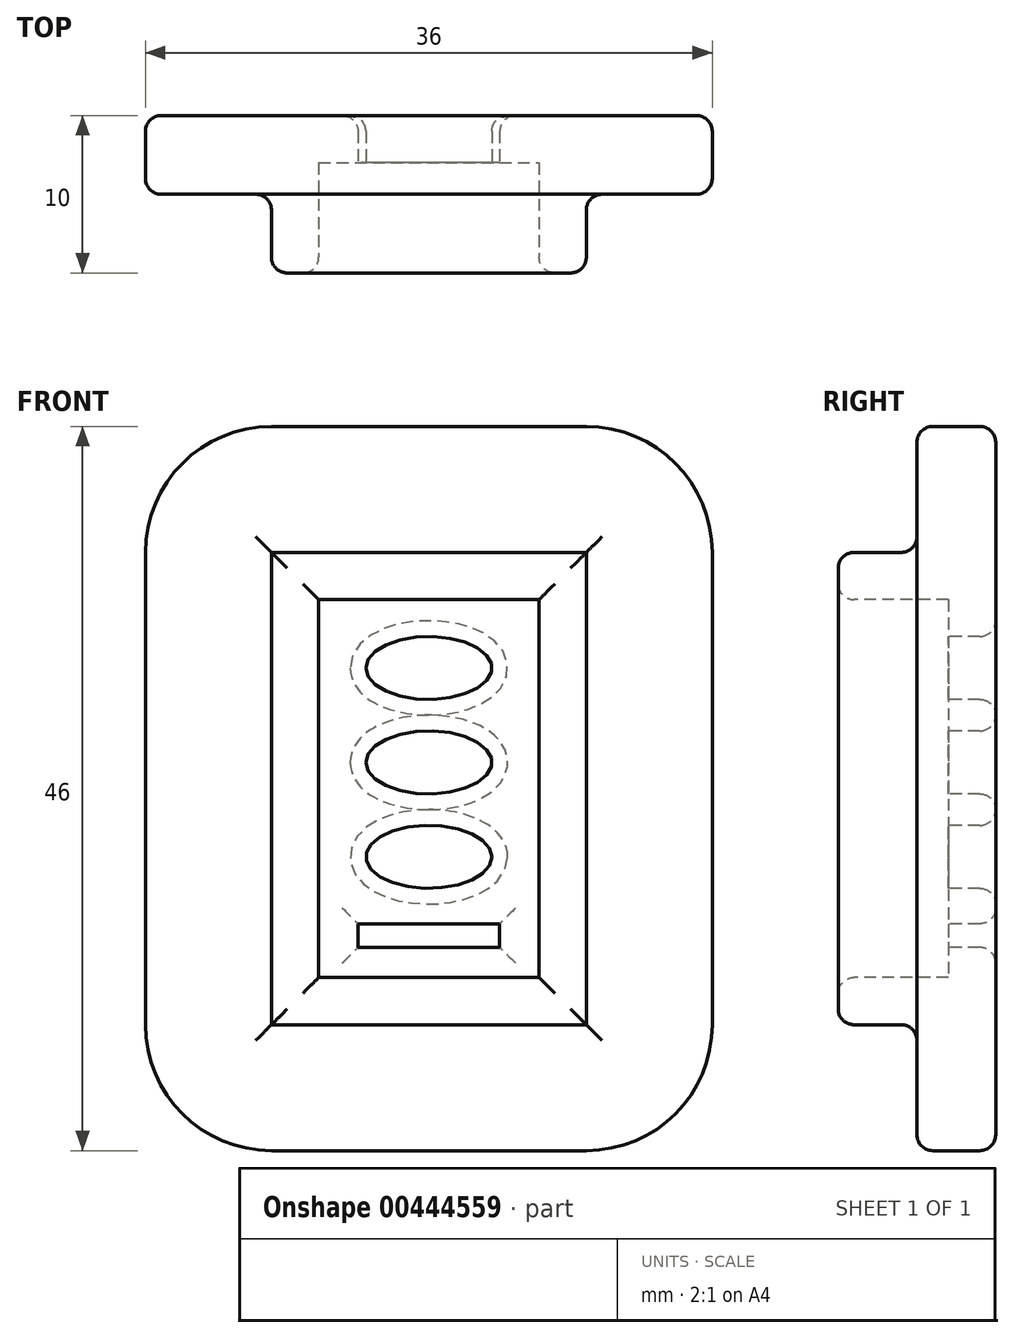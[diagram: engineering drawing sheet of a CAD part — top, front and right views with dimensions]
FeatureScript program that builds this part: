
annotation { "Feature Type Name" : "Feature", "Feature Type Description" : "" }
export const myFeature = defineFeature(function(context is Context, id is Id, definition is map)
    precondition{}
    {
        {
            var Q0;
            Q0=qCreatedBy(makeId("Front.planeOp"),FACE);
            var sketch = newSketch(context, id + "F0", { "sketchPlane" : qUnion([Q0])});
            skLineSegment(sketch, "E0.bottom", {"start": v(-10, -23) * mm, "end": v(10, -23) * mm});
            skLineSegment(sketch, "E0.top", {"start": v(-10, 23) * mm, "end": v(10, 23) * mm});
            skLineSegment(sketch, "E0.left", {"start": v(-18, -15) * mm, "end": v(-18, 15) * mm});
            skLineSegment(sketch, "E0.right", {"start": v(18, -15) * mm, "end": v(18, 15) * mm});
            skPoint(sketch, "E0.middle", {"position": v(0, 0) * mm});
            skPoint(sketch, "E1.visualSharp", {"position": v(-18, 23) * mm});
            skArc(sketch, "E1.filletArc", {"start": v(-10, 23) * mm, "mid": v(-15.66, 20.66) * mm, "end": v(-18, 15) * mm});
            skPoint(sketch, "E2.visualSharp", {"position": v(18, 23) * mm});
            skArc(sketch, "E2.filletArc", {"start": v(18, 15) * mm, "mid": v(15.66, 20.66) * mm, "end": v(10, 23) * mm});
            skPoint(sketch, "E3.visualSharp", {"position": v(18, -23) * mm});
            skArc(sketch, "E3.filletArc", {"start": v(10, -23) * mm, "mid": v(15.66, -20.66) * mm, "end": v(18, -15) * mm});
            skPoint(sketch, "E4.visualSharp", {"position": v(-18, -23) * mm});
            skArc(sketch, "E4.filletArc", {"start": v(-18, -15) * mm, "mid": v(-15.66, -20.66) * mm, "end": v(-10, -23) * mm});
            skSolve(sketch);
        }
        {
            var Q0;
            Q0=makeQuery(id+"F0.imprint","IMPRINT",FACE,{"disambiguationData":[TD([[makeQuery(id+"F0.imprint","IMPRINT",EDGE,{"derivedFrom":sQuery(id+"F0.wireOp",EDGE,"E0.bottom")}),1.0]])]});
            cPlane(context, id + "F1", {"entities" : qUnion([Q0]), "cplaneType" : CPlaneType.OFFSET, "offset" : 5 * mm, "width" : 150 * mm, "height" : 150 * mm});
        }
        {
            var Q0;
            Q0=qCreatedBy(id+"F1.planeOp",FACE);
            var sketch = newSketch(context, id + "F2", { "sketchPlane" : qUnion([Q0])});
            skLineSegment(sketch, "E5.bottom", {"start": v(-10, 15) * mm, "end": v(10, 15) * mm});
            skLineSegment(sketch, "E5.top", {"start": v(-10, -15) * mm, "end": v(10, -15) * mm});
            skLineSegment(sketch, "E5.left", {"start": v(-10, 15) * mm, "end": v(-10, -15) * mm});
            skLineSegment(sketch, "E5.right", {"start": v(10, 15) * mm, "end": v(10, -15) * mm});
            skPoint(sketch, "E5.middle", {"position": v(0, 0) * mm});
            skSolve(sketch);
        }
        {
            var Q0;
            Q0 = qSketchRegion(id + "F2", true);
            extrude(context, id + "F3", {"entities" : qUnion([Q0]), "oppositeDirection" : true, "depth" : 5 * mm});
        }
        {
            var Q0;
            Q0=makeQuery(id+"F3.opExtrude","CAP_FACE",FACE,{"disambiguationData":[OSD([sQuery(id+"F2.wireOp",EDGE,"E5.bottom"),sQuery(id+"F2.wireOp",EDGE,"E5.top"),sQuery(id+"F2.wireOp",EDGE,"E5.left"),sQuery(id+"F2.wireOp",EDGE,"E5.right")])],"isStart":true});
            var Q1;
            Q1=makeQuery(id+"F0.imprint","IMPRINT",FACE,{"disambiguationData":[TD([[makeQuery(id+"F0.imprint","IMPRINT",EDGE,{"derivedFrom":sQuery(id+"F0.wireOp",EDGE,"E0.bottom")}),1.0]])]});
            extrude(context, id + "F4", {"entities" : qUnion([Q0, Q1]), "operationType" : NewBodyOperationType.ADD, "oppositeDirection" : true, "depth" : 5 * mm});
        }
        {
            var Q0;
            Q0=makeQuery(id+"F3.opExtrude","CAP_FACE",FACE,{"disambiguationData":[OSD([sQuery(id+"F2.wireOp",EDGE,"E5.bottom"),sQuery(id+"F2.wireOp",EDGE,"E5.top"),sQuery(id+"F2.wireOp",EDGE,"E5.left"),sQuery(id+"F2.wireOp",EDGE,"E5.right")])],"isStart":true});
            shell(context, id + "F5", {"entities" : qUnion([Q0]), "thickness" : 3 * mm});
        }
        {
            var Q0;
            Q0=makeQuery(id+"F5.opShell","OFFSET_FACE",FACE,{"disambiguationData":[OSD([sQuery(id+"F0.wireOp",EDGE,"E0.bottom"),sQuery(id+"F0.wireOp",EDGE,"E0.top"),sQuery(id+"F0.wireOp",EDGE,"E0.left"),sQuery(id+"F0.wireOp",EDGE,"E0.right"),sQuery(id+"F0.wireOp",EDGE,"E1.filletArc"),sQuery(id+"F0.wireOp",EDGE,"E2.filletArc"),sQuery(id+"F0.wireOp",EDGE,"E3.filletArc"),sQuery(id+"F0.wireOp",EDGE,"E4.filletArc")])]});
            var sketch = newSketch(context, id + "F6", { "sketchPlane" : qUnion([Q0])});
            skLineSegment(sketch, "E6.bottom", {"start": v(4.5, -8.59) * mm, "end": v(-4.5, -8.59) * mm});
            skLineSegment(sketch, "E6.top", {"start": v(4.5, -10.09) * mm, "end": v(-4.5, -10.09) * mm});
            skLineSegment(sketch, "E6.left", {"start": v(4.5, -8.59) * mm, "end": v(4.5, -10.09) * mm});
            skLineSegment(sketch, "E6.right", {"start": v(-4.5, -8.59) * mm, "end": v(-4.5, -10.09) * mm});
            skPoint(sketch, "E6.middle", {"position": v(0, -9.34) * mm});
            skEllipse(sketch, "E7", {"center": v(0, -4.34) * mm, "majorRadius": 4 * mm, "minorRadius": 2 * mm, "majorAxis": v(1, 0)});
            skEllipse(sketch, "E8", {"center": v(0, 1.66) * mm, "majorRadius": 4 * mm, "minorRadius": 2 * mm, "majorAxis": v(-1, 0)});
            skEllipse(sketch, "E9", {"center": v(0, 7.66) * mm, "majorRadius": 4 * mm, "minorRadius": 2 * mm, "majorAxis": v(-1, 0)});
            skSolve(sketch);
        }
        {
            var Q0;
            Q0=makeQuery(id+"F6.imprint","IMPRINT",FACE,{"disambiguationData":[TD([[makeQuery(id+"F6.imprint","IMPRINT",EDGE,{"derivedFrom":sQuery(id+"F6.wireOp",EDGE,"E6.bottom")}),1.0]])]});
            var Q1;
            Q1=makeQuery(id+"F6.imprint","IMPRINT",FACE,{"disambiguationData":[TD([[makeQuery(id+"F6.imprint","IMPRINT",EDGE,{"derivedFrom":sQuery(id+"F6.wireOp",EDGE,"E7")}),1.0]])]});
            var Q2;
            Q2=makeQuery(id+"F6.imprint","IMPRINT",FACE,{"disambiguationData":[TD([[makeQuery(id+"F6.imprint","IMPRINT",EDGE,{"derivedFrom":sQuery(id+"F6.wireOp",EDGE,"E8")}),1.0]])]});
            var Q3;
            Q3=makeQuery(id+"F6.imprint","IMPRINT",FACE,{"disambiguationData":[TD([[makeQuery(id+"F6.imprint","IMPRINT",EDGE,{"derivedFrom":sQuery(id+"F6.wireOp",EDGE,"E9")}),1.0]])]});
            extrude(context, id + "F7", {"entities" : qUnion([Q0, Q1, Q2, Q3]), "operationType" : NewBodyOperationType.REMOVE, "oppositeDirection" : true, "depth" : 3 * mm});
        }
        {
            var Q0;
            Q0=makeQuery(id+"F3.opExtrude","CAP_FACE",FACE,{"disambiguationData":[OSD([sQuery(id+"F2.wireOp",EDGE,"E5.bottom"),sQuery(id+"F2.wireOp",EDGE,"E5.top"),sQuery(id+"F2.wireOp",EDGE,"E5.left"),sQuery(id+"F2.wireOp",EDGE,"E5.right")])],"isStart":true});
            fillet(context, id + "F8", {"entities" : qUnion([Q0]), "radius" : 1 * mm, "tangentPropagation" : true, "allowEdgeOverflow" : false});
        }
        {
            var Q0;
            Q0=makeQuery(id+"F4.opExtrude","CAP_FACE",FACE,{"disambiguationData":[OSD([sQuery(id+"F0.wireOp",EDGE,"E0.bottom"),sQuery(id+"F0.wireOp",EDGE,"E0.top"),sQuery(id+"F0.wireOp",EDGE,"E0.left"),sQuery(id+"F0.wireOp",EDGE,"E0.right"),sQuery(id+"F0.wireOp",EDGE,"E1.filletArc"),sQuery(id+"F0.wireOp",EDGE,"E2.filletArc"),sQuery(id+"F0.wireOp",EDGE,"E3.filletArc"),sQuery(id+"F0.wireOp",EDGE,"E4.filletArc")])],"isStart":true});
            fillet(context, id + "F9", {"entities" : qUnion([Q0]), "radius" : 1 * mm, "tangentPropagation" : true, "allowEdgeOverflow" : false});
        }
        {
            var Q0;
            Q0=makeQuery(id+"F4.opExtrude","CAP_FACE",FACE,{"disambiguationData":[OSD([sQuery(id+"F0.wireOp",EDGE,"E0.bottom"),sQuery(id+"F0.wireOp",EDGE,"E0.top"),sQuery(id+"F0.wireOp",EDGE,"E0.left"),sQuery(id+"F0.wireOp",EDGE,"E0.right"),sQuery(id+"F0.wireOp",EDGE,"E1.filletArc"),sQuery(id+"F0.wireOp",EDGE,"E2.filletArc"),sQuery(id+"F0.wireOp",EDGE,"E3.filletArc"),sQuery(id+"F0.wireOp",EDGE,"E4.filletArc")])],"isStart":false});
            fillet(context, id + "F10", {"entities" : qUnion([Q0]), "radius" : 1 * mm, "tangentPropagation" : true, "allowEdgeOverflow" : false});
        }
    });
